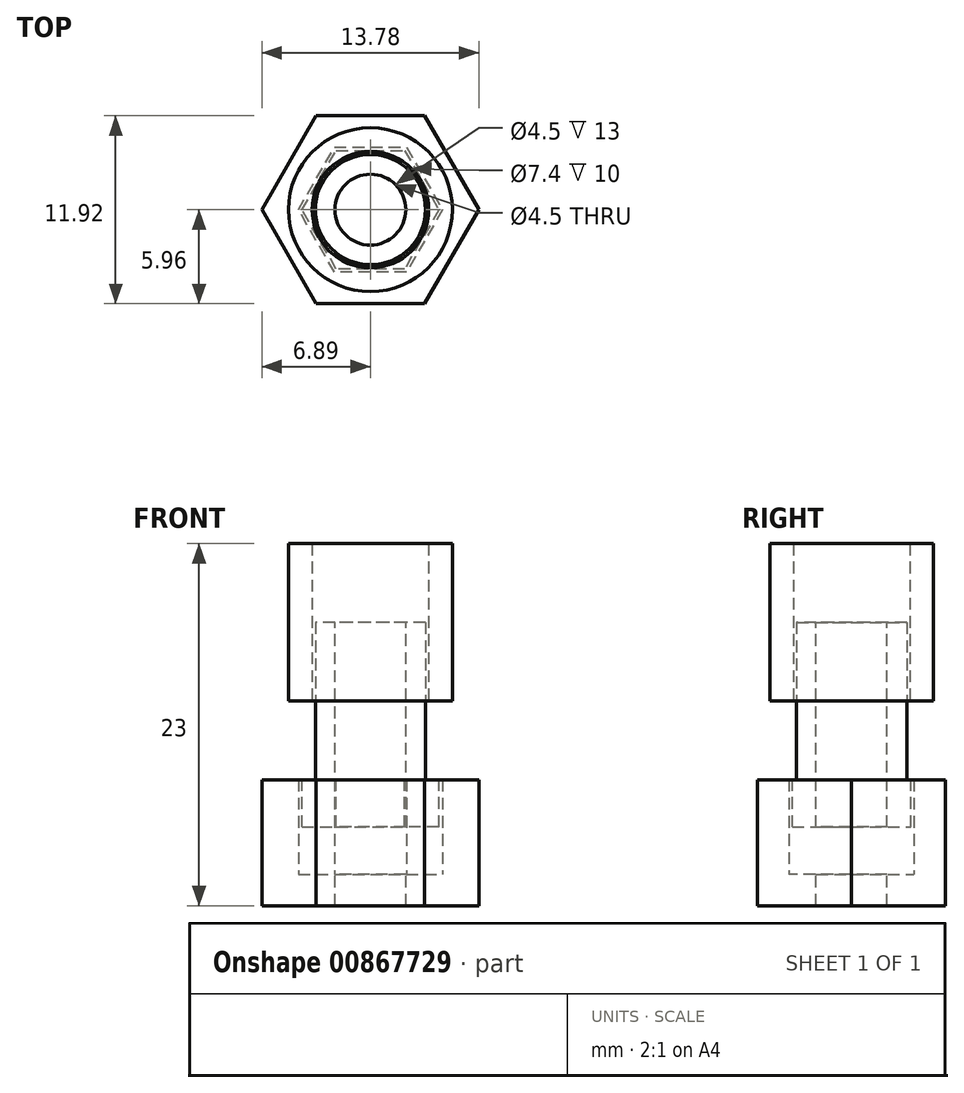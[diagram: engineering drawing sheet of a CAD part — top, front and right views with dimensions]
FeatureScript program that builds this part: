
annotation { "Feature Type Name" : "Feature", "Feature Type Description" : "" }
export const myFeature = defineFeature(function(context is Context, id is Id, definition is map)
    precondition{}
    {
        {
            var Q0;
            Q0=qCreatedBy(makeId("Top.planeOp"),FACE);
            var sketch = newSketch(context, id + "F0", { "sketchPlane" : qUnion([Q0])});
            skCircle(sketch, "E0.cCircle", {"center": v(0, 0) * mm, "radius": 4 * mm, "construction": true});
            skLineSegment(sketch, "E0.0", {"start": v(4, 0) * mm, "end": v(2, -3.46) * mm});
            skLineSegment(sketch, "E0.1", {"start": v(2, -3.46) * mm, "end": v(-2, -3.46) * mm});
            skLineSegment(sketch, "E0.2", {"start": v(-2, -3.46) * mm, "end": v(-4, 0) * mm});
            skLineSegment(sketch, "E0.3", {"start": v(-4, 0) * mm, "end": v(-2, 3.46) * mm});
            skLineSegment(sketch, "E0.4", {"start": v(-2, 3.46) * mm, "end": v(2, 3.46) * mm});
            skLineSegment(sketch, "E0.5", {"start": v(2, 3.46) * mm, "end": v(4, 0) * mm});
            skLineSegment(sketch, "E1.0", {"start": v(-3.44, 5.96) * mm, "end": v(3.44, 5.96) * mm});
            skLineSegment(sketch, "E1.1", {"start": v(6.89, 0) * mm, "end": v(3.44, -5.96) * mm});
            skLineSegment(sketch, "E1.2", {"start": v(3.44, -5.96) * mm, "end": v(-3.44, -5.96) * mm});
            skLineSegment(sketch, "E1.3", {"start": v(3.44, 5.96) * mm, "end": v(6.89, 0) * mm});
            skLineSegment(sketch, "E1.4", {"start": v(-3.44, -5.96) * mm, "end": v(-6.89, 0) * mm});
            skLineSegment(sketch, "E1.5", {"start": v(-6.89, 0) * mm, "end": v(-3.44, 5.96) * mm});
            skLineSegment(sketch, "E2.0", {"start": v(-4.58, 0) * mm, "end": v(-2.29, 3.96) * mm});
            skLineSegment(sketch, "E2.1", {"start": v(2.29, 3.96) * mm, "end": v(4.58, 0) * mm});
            skLineSegment(sketch, "E2.2", {"start": v(4.58, 0) * mm, "end": v(2.29, -3.96) * mm});
            skLineSegment(sketch, "E2.3", {"start": v(-2.29, 3.96) * mm, "end": v(2.29, 3.96) * mm});
            skLineSegment(sketch, "E2.4", {"start": v(2.29, -3.96) * mm, "end": v(-2.29, -3.96) * mm});
            skLineSegment(sketch, "E2.5", {"start": v(-2.29, -3.96) * mm, "end": v(-4.58, 0) * mm});
            skCircle(sketch, "E3", {"center": v(0, 0) * mm, "radius": 2.25 * mm});
            skSolve(sketch);
        }
        {
            var Q0;
            Q0=makeQuery(id+"F0.imprint","IMPRINT",FACE,{"disambiguationData":[TD([[makeQuery(id+"F0.imprint","IMPRINT",EDGE,{"derivedFrom":sQuery(id+"F0.wireOp",EDGE,"E1.0")}),-1.0]])]});
            extrude(context, id + "F1", {"entities" : qUnion([Q0]), "depth" : 6 * mm, "offsetDistance" : 25 * mm});
        }
        {
            var Q0;
            Q0=makeQuery(id+"F0.imprint","IMPRINT",FACE,{"disambiguationData":[TD([[makeQuery(id+"F0.imprint","IMPRINT",EDGE,{"derivedFrom":sQuery(id+"F0.wireOp",EDGE,"E1.0")}),-1.0]])]});
            var Q1;
            Q1=makeQuery(id+"F0.imprint","IMPRINT",FACE,{"disambiguationData":[TD([[makeQuery(id+"F0.imprint","IMPRINT",EDGE,{"derivedFrom":sQuery(id+"F0.wireOp",EDGE,"E0.0")}),1.0]])]});
            var Q2;
            Q2=makeQuery(id+"F0.imprint","IMPRINT",FACE,{"disambiguationData":[TD([[makeQuery(id+"F0.imprint","IMPRINT",EDGE,{"derivedFrom":sQuery(id+"F0.wireOp",EDGE,"E0.0")}),-1.0]])]});
            extrude(context, id + "F2", {"entities" : qUnion([Q0, Q1, Q2]), "operationType" : NewBodyOperationType.ADD, "oppositeDirection" : true, "depth" : 2 * mm, "offsetDistance" : 25 * mm});
        }
        {
            var Q0;
            Q0=makeQuery(id+"F1.opExtrude","CAP_FACE",FACE,{"disambiguationData":[OSD([sQuery(id+"F0.wireOp",EDGE,"E1.0"),sQuery(id+"F0.wireOp",EDGE,"E1.1"),sQuery(id+"F0.wireOp",EDGE,"E1.2"),sQuery(id+"F0.wireOp",EDGE,"E1.3"),sQuery(id+"F0.wireOp",EDGE,"E1.4"),sQuery(id+"F0.wireOp",EDGE,"E1.5"),sQuery(id+"F0.wireOp",EDGE,"E2.0"),sQuery(id+"F0.wireOp",EDGE,"E2.1"),sQuery(id+"F0.wireOp",EDGE,"E2.2"),sQuery(id+"F0.wireOp",EDGE,"E2.3"),sQuery(id+"F0.wireOp",EDGE,"E2.4"),sQuery(id+"F0.wireOp",EDGE,"E2.5")])],"isStart":false});
            var sketch = newSketch(context, id + "F3", { "sketchPlane" : qUnion([Q0])});
            skLineSegment(sketch, "E4.0.0", {"start": v(-6.89, 0) * mm, "end": v(-3.44, -5.96) * mm});
            skLineSegment(sketch, "E4.0.1", {"start": v(-3.44, -5.96) * mm, "end": v(3.44, -5.96) * mm});
            skLineSegment(sketch, "E4.0.2", {"start": v(3.44, -5.96) * mm, "end": v(6.89, 0) * mm});
            skLineSegment(sketch, "E4.0.3", {"start": v(6.89, 0) * mm, "end": v(3.44, 5.96) * mm});
            skLineSegment(sketch, "E4.0.4", {"start": v(3.44, 5.96) * mm, "end": v(-3.44, 5.96) * mm});
            skLineSegment(sketch, "E4.0.5", {"start": v(-3.44, 5.96) * mm, "end": v(-6.89, 0) * mm});
            skLineSegment(sketch, "E5.0", {"start": v(-2.29, 3.96) * mm, "end": v(2.29, 3.96) * mm, "construction": true});
            skLineSegment(sketch, "E6.0", {"start": v(-4.58, 0) * mm, "end": v(-2.29, 3.96) * mm, "construction": true});
            skLineSegment(sketch, "E7.0", {"start": v(-2.29, -3.96) * mm, "end": v(-4.58, 0) * mm, "construction": true});
            skLineSegment(sketch, "E8.0", {"start": v(2.29, -3.96) * mm, "end": v(-2.29, -3.96) * mm, "construction": true});
            skLineSegment(sketch, "E9.0", {"start": v(4.58, 0) * mm, "end": v(2.29, -3.96) * mm, "construction": true});
            skLineSegment(sketch, "E10.0", {"start": v(2.29, 3.96) * mm, "end": v(4.58, 0) * mm, "construction": true});
            skLineSegment(sketch, "E11.0", {"start": v(-4.35, 0) * mm, "end": v(-2.17, 3.76) * mm});
            skLineSegment(sketch, "E11.1", {"start": v(2.17, 3.76) * mm, "end": v(4.35, 0) * mm});
            skLineSegment(sketch, "E11.2", {"start": v(4.35, 0) * mm, "end": v(2.17, -3.76) * mm});
            skLineSegment(sketch, "E11.3", {"start": v(-2.17, 3.76) * mm, "end": v(2.17, 3.76) * mm});
            skLineSegment(sketch, "E11.4", {"start": v(2.17, -3.76) * mm, "end": v(-2.17, -3.76) * mm});
            skLineSegment(sketch, "E11.5", {"start": v(-2.17, -3.76) * mm, "end": v(-4.35, 0) * mm});
            skCircle(sketch, "E12.0.0", {"center": v(0, 0) * mm, "radius": 2.25 * mm});
            skCircle(sketch, "E13", {"center": v(0, 0) * mm, "radius": 3.5 * mm});
            skSolve(sketch);
        }
        {
            var Q0;
            Q0=makeQuery(id+"F3.imprint","IMPRINT",FACE,{"disambiguationData":[TD([[makeQuery(id+"F3.imprint","IMPRINT",EDGE,{"derivedFrom":sQuery(id+"F3.wireOp",EDGE,"E11.0")}),-1.0]])]});
            var Q1;
            Q1=makeQuery(id+"F3.imprint","IMPRINT",FACE,{"disambiguationData":[TD([[makeQuery(id+"F3.imprint","IMPRINT",EDGE,{"derivedFrom":sQuery(id+"F3.wireOp",EDGE,"E12.0.0")}),-1.0]])]});
            extrude(context, id + "F4", {"entities" : qUnion([Q0, Q1]), "oppositeDirection" : true, "depth" : 3 * mm, "offsetDistance" : 25 * mm});
        }
        {
            var Q0;
            Q0=makeQuery(id+"F3.imprint","IMPRINT",FACE,{"disambiguationData":[TD([[makeQuery(id+"F3.imprint","IMPRINT",EDGE,{"derivedFrom":sQuery(id+"F3.wireOp",EDGE,"E12.0.0")}),-1.0]])]});
            extrude(context, id + "F5", {"entities" : qUnion([Q0]), "operationType" : NewBodyOperationType.ADD, "depth" : 10 * mm, "offsetDistance" : 25 * mm});
        }
        {
            var Q0;
            Q0=makeQuery(id+"F5.opExtrude","CAP_FACE",FACE,{"disambiguationData":[OSD([sQuery(id+"F3.wireOp",EDGE,"E12.0.0"),sQuery(id+"F3.wireOp",EDGE,"E13")])],"isStart":false});
            var sketch = newSketch(context, id + "F6", { "sketchPlane" : qUnion([Q0])});
            skCircle(sketch, "E14.0", {"center": v(0, 0) * mm, "radius": 3.5 * mm, "construction": true});
            skCircle(sketch, "E15.0", {"center": v(0, 0) * mm, "radius": 3.7 * mm});
            skCircle(sketch, "E16.0", {"center": v(0, 0) * mm, "radius": 5.2 * mm});
            skSolve(sketch);
        }
        {
            var Q0;
            Q0=makeQuery(id+"F6.imprint","IMPRINT",FACE,{"disambiguationData":[TD([[makeQuery(id+"F6.imprint","IMPRINT",EDGE,{"derivedFrom":sQuery(id+"F6.wireOp",EDGE,"E15.0")}),-1.0]])]});
            var Q1;
            Q1=sQuery(id+"F6.wireOp",EDGE,"E16.0");
            extrude(context, id + "F7", {"entities" : qUnion([Q0]), "surfaceEntities" : qUnion([Q1]), "depth" : 10 * mm, "offsetDistance" : 25 * mm, "symmetric" : true});
        }
    });
